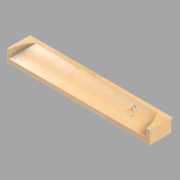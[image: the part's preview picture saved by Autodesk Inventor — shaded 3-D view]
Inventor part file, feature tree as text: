
AUTODESK INVENTOR PART (.ipt)
format: ipt  version: 2022.2 (Build 262287010, 287A)  size: 134,656 bytes
history: native  units: in
note: dims shown in document units (in); Inventor stores cm internally (conversion verified against a paired STEP export)
features: other x1, direct_edit x1, revolve x1
ambient origin geometry x8: Origin, YZ Plane, XZ Plane, XY Plane, X Axis, Y Axis, Z Axis, Center Point
bodies: Solid1 (feature_tree)
feature tree (3):
  other  "North (4) (1)"
  direct_edit  "Direct Edit1"
  revolve  "Rotate1"  Angle=90.0deg
